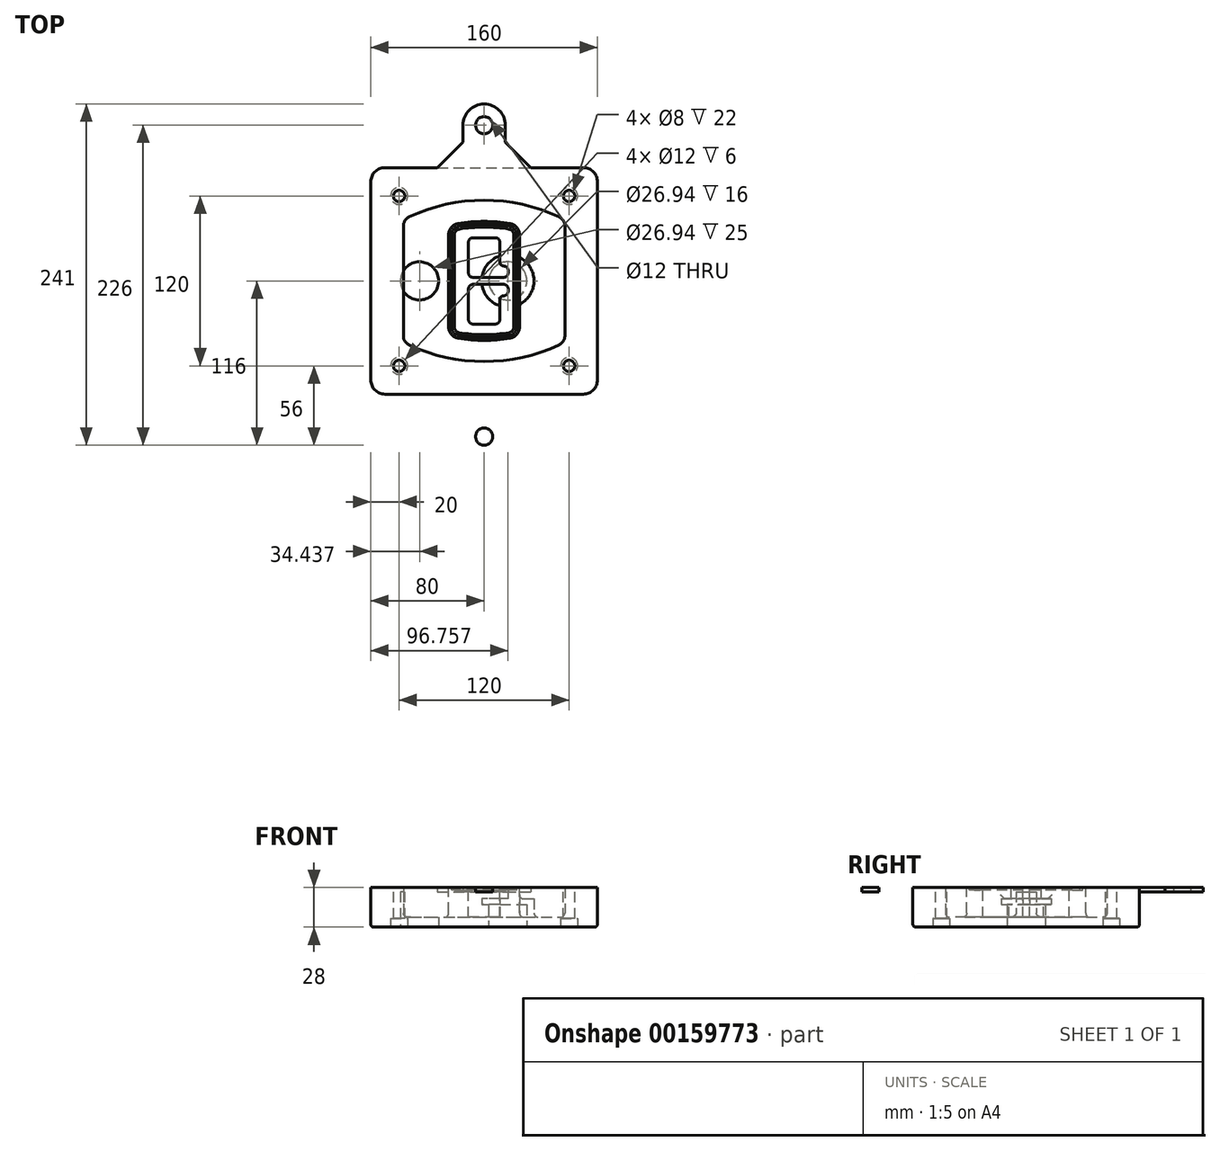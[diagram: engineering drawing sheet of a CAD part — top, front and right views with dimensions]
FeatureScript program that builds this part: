
annotation { "Feature Type Name" : "Feature", "Feature Type Description" : "" }
export const myFeature = defineFeature(function(context is Context, id is Id, definition is map)
    precondition{}
    {
        {
            var Q0;
            Q0=qCreatedBy(makeId("Top.planeOp"),FACE);
            var sketch = newSketch(context, id + "F0", { "sketchPlane" : qUnion([Q0])});
            skPoint(sketch, "E0.rect.middle", {"position": v(0, 0) * mm});
            skLineSegment(sketch, "E1.bottom", {"start": v(-70, -80) * mm, "end": v(70, -80) * mm});
            skLineSegment(sketch, "E1.top", {"start": v(-70, 80) * mm, "end": v(70, 80) * mm});
            skLineSegment(sketch, "E1.left", {"start": v(-80, -70) * mm, "end": v(-80, 70) * mm});
            skLineSegment(sketch, "E1.right", {"start": v(80, -70) * mm, "end": v(80, 70) * mm});
            skLineSegment(sketch, "E2", {"start": v(-80, 80) * mm, "end": v(80, -80) * mm, "construction": true});
            skLineSegment(sketch, "E3", {"start": v(80, 80) * mm, "end": v(-80, -80) * mm, "construction": true});
            skCircle(sketch, "E4", {"center": v(-60, 60) * mm, "radius": 4 * mm});
            skCircle(sketch, "E5", {"center": v(60, 60) * mm, "radius": 4 * mm});
            skCircle(sketch, "E6", {"center": v(60, -60) * mm, "radius": 4 * mm});
            skCircle(sketch, "E7", {"center": v(-60, -60) * mm, "radius": 4 * mm});
            skLineSegment(sketch, "E8", {"start": v(-60, 60) * mm, "end": v(60, 60) * mm, "construction": true});
            skLineSegment(sketch, "E9", {"start": v(60, 60) * mm, "end": v(60, -60) * mm, "construction": true});
            skLineSegment(sketch, "E10", {"start": v(60, -60) * mm, "end": v(-60, -60) * mm, "construction": true});
            skLineSegment(sketch, "E11", {"start": v(-60, -60) * mm, "end": v(-60, 60) * mm, "construction": true});
            skLineSegment(sketch, "E12", {"start": v(-60, 38.83) * mm, "end": v(-60, -38.83) * mm});
            skLineSegment(sketch, "E13", {"start": v(60, 38.83) * mm, "end": v(60, -38.83) * mm});
            skArc(sketch, "E14", {"start": v(54.26, 47.88) * mm, "mid": v(0, 60) * mm, "end": v(-54.26, 47.88) * mm});
            skArc(sketch, "E15", {"start": v(-54.26, -47.88) * mm, "mid": v(0, -60) * mm, "end": v(54.26, -47.88) * mm});
            skLineSegment(sketch, "E16", {"start": v(-60, 0) * mm, "end": v(60, 0) * mm, "construction": true});
            skPoint(sketch, "E17.visualSharp", {"position": v(-60, -45) * mm});
            skArc(sketch, "E17.filletArc", {"start": v(-60, -38.83) * mm, "mid": v(-58.44, -44.2) * mm, "end": v(-54.26, -47.88) * mm});
            skPoint(sketch, "E18.visualSharp", {"position": v(-60, 45) * mm});
            skArc(sketch, "E18.filletArc", {"start": v(-54.26, 47.88) * mm, "mid": v(-58.44, 44.2) * mm, "end": v(-60, 38.83) * mm});
            skPoint(sketch, "E19.visualSharp", {"position": v(60, 45) * mm});
            skArc(sketch, "E19.filletArc", {"start": v(60, 38.83) * mm, "mid": v(58.44, 44.2) * mm, "end": v(54.26, 47.88) * mm});
            skPoint(sketch, "E20.visualSharp", {"position": v(60, -45) * mm});
            skArc(sketch, "E20.filletArc", {"start": v(54.26, -47.88) * mm, "mid": v(58.44, -44.2) * mm, "end": v(60, -38.83) * mm});
            skPoint(sketch, "E21.visualSharp", {"position": v(-80, 80) * mm});
            skArc(sketch, "E21.filletArc", {"start": v(-70, 80) * mm, "mid": v(-77.07, 77.07) * mm, "end": v(-80, 70) * mm});
            skPoint(sketch, "E22.visualSharp", {"position": v(80, 80) * mm});
            skArc(sketch, "E22.filletArc", {"start": v(80, 70) * mm, "mid": v(77.07, 77.07) * mm, "end": v(70, 80) * mm});
            skPoint(sketch, "E23.visualSharp", {"position": v(80, -80) * mm});
            skArc(sketch, "E23.filletArc", {"start": v(70, -80) * mm, "mid": v(77.07, -77.07) * mm, "end": v(80, -70) * mm});
            skPoint(sketch, "E24.visualSharp", {"position": v(-80, -80) * mm});
            skArc(sketch, "E24.filletArc", {"start": v(-80, -70) * mm, "mid": v(-77.07, -77.07) * mm, "end": v(-70, -80) * mm});
            skArc(sketch, "E25.0", {"start": v(57, 38.83) * mm, "mid": v(55.9, 42.58) * mm, "end": v(52.98, 45.17) * mm});
            skLineSegment(sketch, "E25.1", {"start": v(57, 38.83) * mm, "end": v(57, -38.83) * mm});
            skArc(sketch, "E25.2", {"start": v(52.98, -45.17) * mm, "mid": v(55.9, -42.58) * mm, "end": v(57, -38.83) * mm});
            skArc(sketch, "E25.3", {"start": v(-52.98, -45.17) * mm, "mid": v(0, -57) * mm, "end": v(52.98, -45.17) * mm});
            skArc(sketch, "E25.4", {"start": v(-57, -38.83) * mm, "mid": v(-55.9, -42.58) * mm, "end": v(-52.98, -45.17) * mm});
            skArc(sketch, "E25.5", {"start": v(52.98, 45.17) * mm, "mid": v(0, 57) * mm, "end": v(-52.98, 45.17) * mm});
            skLineSegment(sketch, "E25.6", {"start": v(-57, 38.83) * mm, "end": v(-57, -38.83) * mm});
            skArc(sketch, "E25.7", {"start": v(-52.98, 45.17) * mm, "mid": v(-55.9, 42.58) * mm, "end": v(-57, 38.83) * mm});
            skArc(sketch, "E26.0", {"start": v(-55.96, 51.5) * mm, "mid": v(-61.82, 46.33) * mm, "end": v(-64, 38.83) * mm});
            skArc(sketch, "E26.1", {"start": v(55.96, 51.5) * mm, "mid": v(0, 64) * mm, "end": v(-55.96, 51.5) * mm});
            skArc(sketch, "E26.2", {"start": v(64, 38.83) * mm, "mid": v(61.82, 46.33) * mm, "end": v(55.96, 51.5) * mm});
            skLineSegment(sketch, "E26.3", {"start": v(64, 38.83) * mm, "end": v(64, -38.83) * mm});
            skArc(sketch, "E26.4", {"start": v(55.96, -51.5) * mm, "mid": v(61.82, -46.33) * mm, "end": v(64, -38.83) * mm});
            skLineSegment(sketch, "E26.5", {"start": v(-64, 38.83) * mm, "end": v(-64, -38.83) * mm});
            skArc(sketch, "E26.6", {"start": v(-55.96, -51.5) * mm, "mid": v(0, -64) * mm, "end": v(55.96, -51.5) * mm});
            skArc(sketch, "E26.7", {"start": v(-64, -38.83) * mm, "mid": v(-61.82, -46.33) * mm, "end": v(-55.96, -51.5) * mm});
            skSolve(sketch);
        }
        {
            var Q0;
            Q0=makeQuery(id+"F0.imprint","IMPRINT",FACE,{"disambiguationData":[TD([[makeQuery(id+"F0.imprint","IMPRINT",EDGE,{"derivedFrom":sQuery(id+"F0.wireOp",EDGE,"E1.bottom")}),1.0]])]});
            var Q1;
            Q1=makeQuery(id+"F0.imprint","IMPRINT",FACE,{"disambiguationData":[TD([[makeQuery(id+"F0.imprint","IMPRINT",EDGE,{"derivedFrom":sQuery(id+"F0.wireOp",EDGE,"E12")}),1.0]])]});
            var Q2;
            Q2=makeQuery(id+"F0.imprint","IMPRINT",FACE,{"disambiguationData":[TD([[makeQuery(id+"F0.imprint","IMPRINT",EDGE,{"derivedFrom":sQuery(id+"F0.wireOp",EDGE,"E25.0")}),1.0]])]});
            var Q3;
            Q3=makeQuery(id+"F0.imprint","IMPRINT",FACE,{"disambiguationData":[TD([[makeQuery(id+"F0.imprint","IMPRINT",EDGE,{"derivedFrom":sQuery(id+"F0.wireOp",EDGE,"E12")}),-1.0]])]});
            extrude(context, id + "F1", {"entities" : qUnion([Q0, Q1, Q2, Q3]), "oppositeDirection" : true, "depth" : 25 * mm});
        }
        {
            var Q0;
            Q0=makeQuery(id+"F0.imprint","IMPRINT",FACE,{"disambiguationData":[TD([[makeQuery(id+"F0.imprint","IMPRINT",EDGE,{"derivedFrom":sQuery(id+"F0.wireOp",EDGE,"E12")}),1.0]])]});
            extrude(context, id + "F2", {"entities" : qUnion([Q0]), "operationType" : NewBodyOperationType.ADD, "depth" : 3 * mm});
        }
        {
            var Q0;
            Q0=makeQuery(id+"F0.imprint","IMPRINT",FACE,{"disambiguationData":[TD([[makeQuery(id+"F0.imprint","IMPRINT",EDGE,{"derivedFrom":sQuery(id+"F0.wireOp",EDGE,"E25.0")}),1.0]])]});
            extrude(context, id + "F3", {"entities" : qUnion([Q0]), "operationType" : NewBodyOperationType.REMOVE, "oppositeDirection" : true, "depth" : 18 * mm});
        }
        {
            var Q0;
            Q0=makeQuery(id+"F2.opExtrude","CAP_FACE",FACE,{"disambiguationData":[OSD([sQuery(id+"F0.wireOp",EDGE,"E12"),sQuery(id+"F0.wireOp",EDGE,"E13"),sQuery(id+"F0.wireOp",EDGE,"E14"),sQuery(id+"F0.wireOp",EDGE,"E15"),sQuery(id+"F0.wireOp",EDGE,"E17.filletArc"),sQuery(id+"F0.wireOp",EDGE,"E18.filletArc"),sQuery(id+"F0.wireOp",EDGE,"E19.filletArc"),sQuery(id+"F0.wireOp",EDGE,"E20.filletArc"),sQuery(id+"F0.wireOp",EDGE,"E25.0"),sQuery(id+"F0.wireOp",EDGE,"E25.1"),sQuery(id+"F0.wireOp",EDGE,"E25.2"),sQuery(id+"F0.wireOp",EDGE,"E25.3"),sQuery(id+"F0.wireOp",EDGE,"E25.4"),sQuery(id+"F0.wireOp",EDGE,"E25.5"),sQuery(id+"F0.wireOp",EDGE,"E25.6"),sQuery(id+"F0.wireOp",EDGE,"E25.7")])],"isStart":false});
            var sketch = newSketch(context, id + "F4", { "sketchPlane" : qUnion([Q0])});
            skArc(sketch, "E27.0", {"start": v(-18.34, -40.45) * mm, "mid": v(0, -42) * mm, "end": v(18.34, -40.45) * mm});
            skArc(sketch, "E28.0", {"start": v(18.34, 40.45) * mm, "mid": v(0, 42) * mm, "end": v(-18.34, 40.45) * mm});
            skLineSegment(sketch, "E29", {"start": v(-25, 32.57) * mm, "end": v(-25, -32.57) * mm});
            skLineSegment(sketch, "E30", {"start": v(25, 32.57) * mm, "end": v(25, -32.57) * mm});
            skLineSegment(sketch, "E31", {"start": v(-25, 39.1) * mm, "end": v(25, 39.1) * mm, "construction": true});
            skLineSegment(sketch, "E32", {"start": v(-25, -39.1) * mm, "end": v(25, -39.1) * mm, "construction": true});
            skPoint(sketch, "E33.visualSharp", {"position": v(-25, 39.1) * mm});
            skArc(sketch, "E33.filletArc", {"start": v(-18.34, 40.45) * mm, "mid": v(-23.11, 37.73) * mm, "end": v(-25, 32.57) * mm});
            skPoint(sketch, "E34.visualSharp", {"position": v(25, 39.1) * mm});
            skArc(sketch, "E34.filletArc", {"start": v(25, 32.57) * mm, "mid": v(23.11, 37.73) * mm, "end": v(18.34, 40.45) * mm});
            skPoint(sketch, "E35.visualSharp", {"position": v(25, -39.1) * mm});
            skArc(sketch, "E35.filletArc", {"start": v(18.34, -40.45) * mm, "mid": v(23.11, -37.73) * mm, "end": v(25, -32.57) * mm});
            skPoint(sketch, "E36.visualSharp", {"position": v(-25, -39.1) * mm});
            skArc(sketch, "E36.filletArc", {"start": v(-25, -32.57) * mm, "mid": v(-23.11, -37.73) * mm, "end": v(-18.34, -40.45) * mm});
            skArc(sketch, "E37.0", {"start": v(52.98, 45.17) * mm, "mid": v(0, 57) * mm, "end": v(-52.98, 45.17) * mm});
            skArc(sketch, "E37.1", {"start": v(-52.98, 45.17) * mm, "mid": v(-55.9, 42.58) * mm, "end": v(-57, 38.83) * mm});
            skLineSegment(sketch, "E37.2", {"start": v(-57, 38.83) * mm, "end": v(-57, -38.83) * mm});
            skArc(sketch, "E37.3", {"start": v(-57, -38.83) * mm, "mid": v(-55.9, -42.58) * mm, "end": v(-52.98, -45.17) * mm});
            skArc(sketch, "E37.4", {"start": v(-52.98, -45.17) * mm, "mid": v(0, -57) * mm, "end": v(52.98, -45.17) * mm});
            skArc(sketch, "E37.5", {"start": v(52.98, -45.17) * mm, "mid": v(55.9, -42.58) * mm, "end": v(57, -38.83) * mm});
            skLineSegment(sketch, "E37.6", {"start": v(57, 38.83) * mm, "end": v(57, -38.83) * mm});
            skArc(sketch, "E37.7", {"start": v(57, 38.83) * mm, "mid": v(55.9, 42.58) * mm, "end": v(52.98, 45.17) * mm});
            skLineSegment(sketch, "E38.0", {"start": v(23, 32.57) * mm, "end": v(23, -32.57) * mm});
            skArc(sketch, "E38.1", {"start": v(18, -38.48) * mm, "mid": v(21.58, -36.44) * mm, "end": v(23, -32.57) * mm});
            skArc(sketch, "E38.2", {"start": v(-18, -38.48) * mm, "mid": v(0, -40) * mm, "end": v(18, -38.48) * mm});
            skArc(sketch, "E38.3", {"start": v(-23, -32.57) * mm, "mid": v(-21.58, -36.44) * mm, "end": v(-18, -38.48) * mm});
            skLineSegment(sketch, "E38.4", {"start": v(-23, 32.57) * mm, "end": v(-23, -32.57) * mm});
            skArc(sketch, "E38.5", {"start": v(23, 32.57) * mm, "mid": v(21.58, 36.44) * mm, "end": v(18, 38.48) * mm});
            skArc(sketch, "E38.6", {"start": v(-18, 38.48) * mm, "mid": v(-21.58, 36.44) * mm, "end": v(-23, 32.57) * mm});
            skArc(sketch, "E38.7", {"start": v(18, 38.48) * mm, "mid": v(0, 40) * mm, "end": v(-18, 38.48) * mm});
            skArc(sketch, "E39.0", {"start": v(21, 32.57) * mm, "mid": v(20.06, 35.15) * mm, "end": v(17.67, 36.5) * mm});
            skLineSegment(sketch, "E39.1", {"start": v(21, 32.57) * mm, "end": v(21, -32.57) * mm});
            skArc(sketch, "E39.2", {"start": v(17.67, -36.5) * mm, "mid": v(20.06, -35.15) * mm, "end": v(21, -32.57) * mm});
            skArc(sketch, "E39.3", {"start": v(-17.67, -36.5) * mm, "mid": v(0, -38) * mm, "end": v(17.67, -36.5) * mm});
            skArc(sketch, "E39.4", {"start": v(-21, -32.57) * mm, "mid": v(-20.06, -35.15) * mm, "end": v(-17.67, -36.5) * mm});
            skArc(sketch, "E39.5", {"start": v(17.67, 36.5) * mm, "mid": v(0, 38) * mm, "end": v(-17.67, 36.5) * mm});
            skLineSegment(sketch, "E39.6", {"start": v(-21, 32.57) * mm, "end": v(-21, -32.57) * mm});
            skArc(sketch, "E39.7", {"start": v(-17.67, 36.5) * mm, "mid": v(-20.06, 35.15) * mm, "end": v(-21, 32.57) * mm});
            skLineSegment(sketch, "E40", {"start": v(-25, 0) * mm, "end": v(25, 0) * mm, "construction": true});
            skLineSegment(sketch, "E41", {"start": v(-11, 5.5) * mm, "end": v(-11, 27.5) * mm});
            skLineSegment(sketch, "E42", {"start": v(-8, 30.5) * mm, "end": v(8, 30.5) * mm});
            skLineSegment(sketch, "E43", {"start": v(11, 27.5) * mm, "end": v(11, 13.5) * mm});
            skLineSegment(sketch, "E44", {"start": v(14, 10.5) * mm, "end": v(14, 10.5) * mm});
            skLineSegment(sketch, "E45", {"start": v(17, 7.5) * mm, "end": v(17, 5.5) * mm});
            skLineSegment(sketch, "E46", {"start": v(14, 2.5) * mm, "end": v(-8, 2.5) * mm});
            skPoint(sketch, "E47.visualSharp", {"position": v(-11, 30.5) * mm});
            skArc(sketch, "E47.filletArc", {"start": v(-8, 30.5) * mm, "mid": v(-10.12, 29.62) * mm, "end": v(-11, 27.5) * mm});
            skPoint(sketch, "E48.visualSharp", {"position": v(11, 30.5) * mm});
            skArc(sketch, "E48.filletArc", {"start": v(11, 27.5) * mm, "mid": v(10.12, 29.62) * mm, "end": v(8, 30.5) * mm});
            skPoint(sketch, "E49.visualSharp", {"position": v(11, 10.5) * mm});
            skArc(sketch, "E49.filletArc", {"start": v(11, 13.5) * mm, "mid": v(11.88, 11.38) * mm, "end": v(14, 10.5) * mm});
            skPoint(sketch, "E50.visualSharp", {"position": v(17, 10.5) * mm});
            skArc(sketch, "E50.filletArc", {"start": v(17, 7.5) * mm, "mid": v(16.12, 9.62) * mm, "end": v(14, 10.5) * mm});
            skPoint(sketch, "E51.visualSharp", {"position": v(17, 2.5) * mm});
            skArc(sketch, "E51.filletArc", {"start": v(14, 2.5) * mm, "mid": v(16.12, 3.38) * mm, "end": v(17, 5.5) * mm});
            skPoint(sketch, "E52.visualSharp", {"position": v(-11, 2.5) * mm});
            skArc(sketch, "E52.filletArc", {"start": v(-11, 5.5) * mm, "mid": v(-10.12, 3.38) * mm, "end": v(-8, 2.5) * mm});
            skLineSegment(sketch, "E53.0.MirrorCS", {"start": v(14, -2.5) * mm, "end": v(-8, -2.5) * mm});
            skArc(sketch, "E54.0.MirrorCS", {"start": v(-11, -5.5) * mm, "mid": v(-10.12, -3.38) * mm, "end": v(-8, -2.5) * mm});
            skLineSegment(sketch, "E55.0.MirrorCS", {"start": v(-11, -5.5) * mm, "end": v(-11, -27.5) * mm});
            skArc(sketch, "E56.0.MirrorCS", {"start": v(-8, -30.5) * mm, "mid": v(-10.12, -29.62) * mm, "end": v(-11, -27.5) * mm});
            skLineSegment(sketch, "E57.0.MirrorCS", {"start": v(-8, -30.5) * mm, "end": v(8, -30.5) * mm});
            skArc(sketch, "E58.0.MirrorCS", {"start": v(11, -27.5) * mm, "mid": v(10.12, -29.62) * mm, "end": v(8, -30.5) * mm});
            skLineSegment(sketch, "E59.0.MirrorCS", {"start": v(11, -27.5) * mm, "end": v(11, -13.5) * mm});
            skArc(sketch, "E60.0.MirrorCS", {"start": v(11, -13.5) * mm, "mid": v(11.88, -11.38) * mm, "end": v(14, -10.5) * mm});
            skArc(sketch, "E61.0.MirrorCS", {"start": v(17, -7.5) * mm, "mid": v(16.12, -9.62) * mm, "end": v(14, -10.5) * mm});
            skLineSegment(sketch, "E62.0.MirrorCS", {"start": v(17, -7.5) * mm, "end": v(17, -5.5) * mm});
            skArc(sketch, "E63.0.MirrorCS", {"start": v(14, -2.5) * mm, "mid": v(16.12, -3.38) * mm, "end": v(17, -5.5) * mm});
            skSolve(sketch);
        }
        {
            var Q0;
            Q0=makeQuery(id+"F4.imprint","IMPRINT",FACE,{"disambiguationData":[TD([[makeQuery(id+"F4.imprint","IMPRINT",EDGE,{"derivedFrom":sQuery(id+"F4.wireOp",EDGE,"E27.0")}),1.0]])]});
            var Q1;
            Q1=makeQuery(id+"F4.imprint","IMPRINT",FACE,{"disambiguationData":[TD([[makeQuery(id+"F4.imprint","IMPRINT",EDGE,{"derivedFrom":sQuery(id+"F4.wireOp",EDGE,"E38.0")}),-1.0]])]});
            var Q2;
            Q2=makeQuery(id+"F4.imprint","IMPRINT",FACE,{"disambiguationData":[TD([[makeQuery(id+"F4.imprint","IMPRINT",EDGE,{"derivedFrom":sQuery(id+"F4.wireOp",EDGE,"E39.0")}),1.0]])]});
            extrude(context, id + "F5", {"entities" : qUnion([Q0, Q1, Q2]), "operationType" : NewBodyOperationType.ADD, "endBound" : BoundingType.UP_TO_NEXT, "oppositeDirection" : true, "depth" : 25 * mm});
        }
        {
            var Q0;
            Q0=makeQuery(id+"F4.imprint","IMPRINT",FACE,{"disambiguationData":[TD([[makeQuery(id+"F4.imprint","IMPRINT",EDGE,{"derivedFrom":sQuery(id+"F4.wireOp",EDGE,"E38.0")}),-1.0]])]});
            extrude(context, id + "F6", {"entities" : qUnion([Q0]), "operationType" : NewBodyOperationType.REMOVE, "oppositeDirection" : true, "depth" : 2 * mm});
        }
        {
            var Q0;
            Q0=makeQuery(id+"F1.opExtrude","CAP_FACE",FACE,{"disambiguationData":[OSD([sQuery(id+"F0.wireOp",EDGE,"E1.bottom"),sQuery(id+"F0.wireOp",EDGE,"E1.top"),sQuery(id+"F0.wireOp",EDGE,"E1.left"),sQuery(id+"F0.wireOp",EDGE,"E1.right"),sQuery(id+"F0.wireOp",EDGE,"E4"),sQuery(id+"F0.wireOp",EDGE,"E5"),sQuery(id+"F0.wireOp",EDGE,"E6"),sQuery(id+"F0.wireOp",EDGE,"E7"),sQuery(id+"F0.wireOp",EDGE,"E21.filletArc"),sQuery(id+"F0.wireOp",EDGE,"E22.filletArc"),sQuery(id+"F0.wireOp",EDGE,"E23.filletArc"),sQuery(id+"F0.wireOp",EDGE,"E24.filletArc")])],"isStart":false});
            var sketch = newSketch(context, id + "F7", { "sketchPlane" : qUnion([Q0])});
            skCircle(sketch, "E64", {"center": v(16.76, 0) * mm, "radius": 13.47 * mm});
            skCircle(sketch, "E65", {"center": v(-45.56, 0) * mm, "radius": 13.47 * mm});
            skLineSegment(sketch, "E66", {"start": v(80, 0) * mm, "end": v(-80, 0) * mm});
            skCircle(sketch, "E67", {"center": v(16.76, 0) * mm, "radius": 18.47 * mm});
            skCircle(sketch, "E68", {"center": v(60, -60) * mm, "radius": 6 * mm});
            skCircle(sketch, "E69", {"center": v(-60, -60) * mm, "radius": 6 * mm});
            skCircle(sketch, "E70", {"center": v(-60, 60) * mm, "radius": 6 * mm});
            skCircle(sketch, "E71", {"center": v(60, 60) * mm, "radius": 6 * mm});
            skSolve(sketch);
        }
        {
            var Q0;
            {var subQ1=sQuery(id+"F7.wireOp",EDGE,"E66");var subQ4=sQuery(id+"F7.wireOp",EDGE,"E64");var subQ6=makeQuery(id+"F7.imprint","INTERSECT",VERTEX,{"disambiguationData":[OD(0.0)],"derivedFrom":[subQ4,subQ1]});Q0=makeQuery(id+"F7.imprint","IMPRINT",FACE,{"disambiguationData":[TD([[makeQuery(id+"F7.imprint","IMPRINT",EDGE,{"disambiguationData":[TD([[subQ6,-1.0]])],"derivedFrom":subQ4}),-1.0]])]});}
            var Q1;
            {var subQ0=sQuery(id+"F7.wireOp",EDGE,"E66");var subQ1=sQuery(id+"F7.wireOp",EDGE,"E64");var subQ3=makeQuery(id+"F7.imprint","INTERSECT",VERTEX,{"disambiguationData":[OD(0.0)],"derivedFrom":[subQ1,subQ0]});Q1=makeQuery(id+"F7.imprint","IMPRINT",FACE,{"disambiguationData":[TD([[makeQuery(id+"F7.imprint","IMPRINT",EDGE,{"disambiguationData":[TD([[subQ3,-1.0]])],"derivedFrom":subQ1}),1.0]])]});}
            var Q2;
            {var subQ0=sQuery(id+"F7.wireOp",EDGE,"E66");var subQ1=sQuery(id+"F7.wireOp",EDGE,"E64");var subQ3=makeQuery(id+"F7.imprint","INTERSECT",VERTEX,{"disambiguationData":[OD(0.0)],"derivedFrom":[subQ1,subQ0]});Q2=makeQuery(id+"F7.imprint","IMPRINT",FACE,{"disambiguationData":[TD([[makeQuery(id+"F7.imprint","IMPRINT",EDGE,{"disambiguationData":[TD([[subQ3,1.0]])],"derivedFrom":subQ1}),1.0]])]});}
            var Q3;
            {var subQ1=sQuery(id+"F7.wireOp",EDGE,"E66");var subQ4=sQuery(id+"F7.wireOp",EDGE,"E64");var subQ6=makeQuery(id+"F7.imprint","INTERSECT",VERTEX,{"disambiguationData":[OD(0.0)],"derivedFrom":[subQ4,subQ1]});Q3=makeQuery(id+"F7.imprint","IMPRINT",FACE,{"disambiguationData":[TD([[makeQuery(id+"F7.imprint","IMPRINT",EDGE,{"disambiguationData":[TD([[subQ6,1.0]])],"derivedFrom":subQ4}),-1.0]])]});}
            extrude(context, id + "F8", {"entities" : qUnion([Q0, Q1, Q2, Q3]), "operationType" : NewBodyOperationType.ADD, "oppositeDirection" : true, "depth" : 20 * mm});
        }
        {
            var Q0;
            {var subQ0=sQuery(id+"F7.wireOp",EDGE,"E66");var subQ1=sQuery(id+"F7.wireOp",EDGE,"E64");var subQ3=makeQuery(id+"F7.imprint","INTERSECT",VERTEX,{"disambiguationData":[OD(0.0)],"derivedFrom":[subQ1,subQ0]});Q0=makeQuery(id+"F7.imprint","IMPRINT",FACE,{"disambiguationData":[TD([[makeQuery(id+"F7.imprint","IMPRINT",EDGE,{"disambiguationData":[TD([[subQ3,-1.0]])],"derivedFrom":subQ1}),1.0]])]});}
            var Q1;
            {var subQ0=sQuery(id+"F7.wireOp",EDGE,"E66");var subQ1=sQuery(id+"F7.wireOp",EDGE,"E64");var subQ3=makeQuery(id+"F7.imprint","INTERSECT",VERTEX,{"disambiguationData":[OD(0.0)],"derivedFrom":[subQ1,subQ0]});Q1=makeQuery(id+"F7.imprint","IMPRINT",FACE,{"disambiguationData":[TD([[makeQuery(id+"F7.imprint","IMPRINT",EDGE,{"disambiguationData":[TD([[subQ3,1.0]])],"derivedFrom":subQ1}),1.0]])]});}
            extrude(context, id + "F9", {"entities" : qUnion([Q0, Q1]), "operationType" : NewBodyOperationType.REMOVE, "oppositeDirection" : true, "depth" : 16 * mm});
        }
        {
            var Q0;
            {var subQ0=sQuery(id+"F7.wireOp",EDGE,"E66");var subQ1=sQuery(id+"F7.wireOp",EDGE,"E65");var subQ3=makeQuery(id+"F7.imprint","INTERSECT",VERTEX,{"disambiguationData":[OD(0.0)],"derivedFrom":[subQ1,subQ0]});Q0=makeQuery(id+"F7.imprint","IMPRINT",FACE,{"disambiguationData":[TD([[makeQuery(id+"F7.imprint","IMPRINT",EDGE,{"disambiguationData":[TD([[subQ3,-1.0]])],"derivedFrom":subQ1}),1.0]])]});}
            var Q1;
            {var subQ0=sQuery(id+"F7.wireOp",EDGE,"E66");var subQ1=sQuery(id+"F7.wireOp",EDGE,"E65");var subQ3=makeQuery(id+"F7.imprint","INTERSECT",VERTEX,{"disambiguationData":[OD(0.0)],"derivedFrom":[subQ1,subQ0]});Q1=makeQuery(id+"F7.imprint","IMPRINT",FACE,{"disambiguationData":[TD([[makeQuery(id+"F7.imprint","IMPRINT",EDGE,{"disambiguationData":[TD([[subQ3,1.0]])],"derivedFrom":subQ1}),1.0]])]});}
            extrude(context, id + "F10", {"entities" : qUnion([Q0, Q1]), "operationType" : NewBodyOperationType.REMOVE, "oppositeDirection" : true, "depth" : 25 * mm});
        }
        {
            var Q0;
            Q0=makeQuery(id+"F7.imprint","IMPRINT",FACE,{"disambiguationData":[TD([[makeQuery(id+"F7.imprint","IMPRINT",EDGE,{"derivedFrom":sQuery(id+"F7.wireOp",EDGE,"E68")}),1.0]])]});
            var Q1;
            Q1=makeQuery(id+"F7.imprint","IMPRINT",FACE,{"disambiguationData":[TD([[makeQuery(id+"F7.imprint","IMPRINT",EDGE,{"derivedFrom":makeQuery(id+"F1.opExtrude","CAP_EDGE",EDGE,{"disambiguationData":[OSD([sQuery(id+"F0.wireOp",EDGE,"E5")])],"isStart":false})}),-1.0]])]});
            var Q2;
            Q2=makeQuery(id+"F7.imprint","IMPRINT",FACE,{"disambiguationData":[TD([[makeQuery(id+"F7.imprint","IMPRINT",EDGE,{"derivedFrom":sQuery(id+"F7.wireOp",EDGE,"E69")}),1.0]])]});
            var Q3;
            Q3=makeQuery(id+"F7.imprint","IMPRINT",FACE,{"disambiguationData":[TD([[makeQuery(id+"F7.imprint","IMPRINT",EDGE,{"derivedFrom":makeQuery(id+"F1.opExtrude","CAP_EDGE",EDGE,{"disambiguationData":[OSD([sQuery(id+"F0.wireOp",EDGE,"E4")])],"isStart":false})}),-1.0]])]});
            var Q4;
            Q4=makeQuery(id+"F7.imprint","IMPRINT",FACE,{"disambiguationData":[TD([[makeQuery(id+"F7.imprint","IMPRINT",EDGE,{"derivedFrom":sQuery(id+"F7.wireOp",EDGE,"E70")}),1.0]])]});
            var Q5;
            Q5=makeQuery(id+"F7.imprint","IMPRINT",FACE,{"disambiguationData":[TD([[makeQuery(id+"F7.imprint","IMPRINT",EDGE,{"derivedFrom":makeQuery(id+"F1.opExtrude","CAP_EDGE",EDGE,{"disambiguationData":[OSD([sQuery(id+"F0.wireOp",EDGE,"E7")])],"isStart":false})}),-1.0]])]});
            var Q6;
            Q6=makeQuery(id+"F7.imprint","IMPRINT",FACE,{"disambiguationData":[TD([[makeQuery(id+"F7.imprint","IMPRINT",EDGE,{"derivedFrom":sQuery(id+"F7.wireOp",EDGE,"E71")}),1.0]])]});
            var Q7;
            Q7=makeQuery(id+"F7.imprint","IMPRINT",FACE,{"disambiguationData":[TD([[makeQuery(id+"F7.imprint","IMPRINT",EDGE,{"derivedFrom":makeQuery(id+"F1.opExtrude","CAP_EDGE",EDGE,{"disambiguationData":[OSD([sQuery(id+"F0.wireOp",EDGE,"E6")])],"isStart":false})}),-1.0]])]});
            extrude(context, id + "F11", {"entities" : qUnion([Q0, Q1, Q2, Q3, Q4, Q5, Q6, Q7]), "operationType" : NewBodyOperationType.REMOVE, "oppositeDirection" : true, "depth" : 6 * mm});
        }
        {
            var Q0;
            Q0=makeQuery(id+"F9.boolean.opBoolean","COPY",FACE,{"derivedFrom":makeQuery(id+"F9.opExtrude","CAP_FACE",FACE,{"disambiguationData":[OSD([sQuery(id+"F7.wireOp",EDGE,"E64")])],"isStart":false})});
            var sketch = newSketch(context, id + "F12", { "sketchPlane" : qUnion([Q0])});
            skArc(sketch, "E72.0", {"start": v(11, 17.55) * mm, "mid": v(2.57, 11.82) * mm, "end": v(-1.54, 2.5) * mm});
            skArc(sketch, "E72.1", {"start": v(-1.54, -2.5) * mm, "mid": v(2.57, -11.82) * mm, "end": v(11, -17.55) * mm});
            skLineSegment(sketch, "E73", {"start": v(-1.54, -2.5) * mm, "end": v(14, -2.5) * mm});
            skLineSegment(sketch, "E74.0", {"start": v(14, 2.5) * mm, "end": v(-1.54, 2.5) * mm});
            skArc(sketch, "E74.1", {"start": v(14, 2.5) * mm, "mid": v(16.12, 3.38) * mm, "end": v(17, 5.5) * mm});
            skLineSegment(sketch, "E74.2", {"start": v(17, 7.5) * mm, "end": v(17, 5.5) * mm});
            skArc(sketch, "E74.3", {"start": v(17, 7.5) * mm, "mid": v(16.12, 9.62) * mm, "end": v(14, 10.5) * mm});
            skArc(sketch, "E74.4", {"start": v(11, 13.5) * mm, "mid": v(11.88, 11.38) * mm, "end": v(14, 10.5) * mm});
            skLineSegment(sketch, "E74.5", {"start": v(11, 17.55) * mm, "end": v(11, 13.5) * mm});
            skLineSegment(sketch, "E74.7", {"start": v(14, -2.5) * mm, "end": v(-1.54, -2.5) * mm});
            skArc(sketch, "E74.8", {"start": v(14, -2.5) * mm, "mid": v(16.12, -3.38) * mm, "end": v(17, -5.5) * mm});
            skLineSegment(sketch, "E74.9", {"start": v(17, -7.5) * mm, "end": v(17, -5.5) * mm});
            skArc(sketch, "E74.10", {"start": v(17, -7.5) * mm, "mid": v(16.12, -9.62) * mm, "end": v(14, -10.5) * mm});
            skArc(sketch, "E74.11", {"start": v(11, -13.5) * mm, "mid": v(11.88, -11.38) * mm, "end": v(14, -10.5) * mm});
            skLineSegment(sketch, "E74.12", {"start": v(11, -17.55) * mm, "end": v(11, -13.5) * mm});
            skPoint(sketch, "E75.orphan", {"position": v(11, -27.5) * mm});
            skPoint(sketch, "E76.orphan", {"position": v(-8, -2.5) * mm});
            skPoint(sketch, "E77.orphan", {"position": v(-8, 2.5) * mm});
            skPoint(sketch, "E78.orphan", {"position": v(11, 27.5) * mm});
            skSolve(sketch);
        }
        {
            var Q0;
            {var subQ7=sQuery(id+"F12.wireOp",EDGE,"E72.0");var subQ14=sQuery(id+"F12.wireOp",EDGE,"E72.1");var subQ16=sQuery(id+"F12.wireOp",EDGE,"E74.1");var subQ18=sQuery(id+"F12.wireOp",EDGE,"E74.8");Q0=qUnion([makeQuery(id+"F12.imprint","IMPRINT",FACE,{"disambiguationData":[TD([[makeQuery(id+"F12.imprint","IMPRINT",EDGE,{"derivedFrom":subQ7}),1.0]])]}),makeQuery(id+"F12.imprint","IMPRINT",FACE,{"disambiguationData":[TD([[makeQuery(id+"F12.imprint","IMPRINT",EDGE,{"derivedFrom":subQ14}),1.0]])]}),makeQuery(id+"F12.imprint","IMPRINT",FACE,{"disambiguationData":[TD([[makeQuery(id+"F12.imprint","IMPRINT",EDGE,{"derivedFrom":subQ16}),1.0]])]}),makeQuery(id+"F12.imprint","IMPRINT",FACE,{"disambiguationData":[TD([[makeQuery(id+"F12.imprint","IMPRINT",EDGE,{"derivedFrom":subQ18}),-1.0]])]})]);}
            var Q1;
            Q1=makeQuery(id+"F5.boolean.opBoolean","SPLIT",FACE,{"disambiguationData":[TD([makeQuery(id+"F5.opExtrude","SWEPT_FACE",FACE,{"disambiguationData":[OSD([sQuery(id+"F4.wireOp",EDGE,"E41")])]})])],"derivedFrom":makeQuery(id+"F3.boolean.opBoolean","COPY",FACE,{"derivedFrom":makeQuery(id+"F3.opExtrude","CAP_FACE",FACE,{"disambiguationData":[OSD([sQuery(id+"F0.wireOp",EDGE,"E25.0"),sQuery(id+"F0.wireOp",EDGE,"E25.1"),sQuery(id+"F0.wireOp",EDGE,"E25.2"),sQuery(id+"F0.wireOp",EDGE,"E25.3"),sQuery(id+"F0.wireOp",EDGE,"E25.4"),sQuery(id+"F0.wireOp",EDGE,"E25.5"),sQuery(id+"F0.wireOp",EDGE,"E25.6"),sQuery(id+"F0.wireOp",EDGE,"E25.7")])],"isStart":false})})});
            extrude(context, id + "F13", {"entities" : qUnion([Q0]), "operationType" : NewBodyOperationType.REMOVE, "endBound" : BoundingType.UP_TO_SURFACE, "endBoundEntityFace" : qUnion([Q1]), "depth" : 25 * mm});
        }
        {
            var Q0;
            Q0=makeQuery(id+"F3.boolean.opBoolean","COPY",EDGE,{"derivedFrom":makeQuery(id+"F3.opExtrude","CAP_EDGE",EDGE,{"disambiguationData":[OSD([sQuery(id+"F0.wireOp",EDGE,"E25.6")])],"isStart":false})});
            var Q1;
            Q1=makeQuery(id+"F8.boolean.opBoolean","INTERSECT",EDGE,{"derivedFrom":[makeQuery(id+"F5.opExtrude","SWEPT_FACE",FACE,{"disambiguationData":[OSD([sQuery(id+"F4.wireOp",EDGE,"E30")])]}),makeQuery(id+"F8.opExtrude","CAP_FACE",FACE,{"disambiguationData":[OSD([sQuery(id+"F7.wireOp",EDGE,"E67")])],"isStart":false})]});
            var Q2;
            Q2=makeQuery(id+"F8.boolean.opBoolean","INTERSECT",EDGE,{"disambiguationData":[OD(1.0)],"derivedFrom":[makeQuery(id+"F5.opExtrude","SWEPT_FACE",FACE,{"disambiguationData":[OSD([sQuery(id+"F4.wireOp",EDGE,"E30")])]}),makeQuery(id+"F8.opExtrude","SWEPT_FACE",FACE,{"disambiguationData":[OSD([sQuery(id+"F7.wireOp",EDGE,"E67")])]})]});
            var Q3;
            {var subQ0=sQuery(id+"F4.wireOp",EDGE,"E30");Q3=makeQuery(id+"F8.boolean.opBoolean","SPLIT",EDGE,{"disambiguationData":[TD([makeQuery(id+"F5.opExtrude","SWEPT_FACE",FACE,{"disambiguationData":[OSD([sQuery(id+"F4.wireOp",EDGE,"E35.filletArc")])]})])],"derivedFrom":makeQuery(id+"F5.opExtrude","CAP_EDGE",EDGE,{"disambiguationData":[OSD([subQ0])],"isStart":false})});}
            var Q4;
            {var subQ0=sQuery(id+"F0.wireOp",EDGE,"E25.7");var subQ1=sQuery(id+"F0.wireOp",EDGE,"E25.1");var subQ2=sQuery(id+"F0.wireOp",EDGE,"E25.6");var subQ3=sQuery(id+"F0.wireOp",EDGE,"E25.5");var subQ4=sQuery(id+"F0.wireOp",EDGE,"E25.4");var subQ5=sQuery(id+"F0.wireOp",EDGE,"E25.0");var subQ6=sQuery(id+"F0.wireOp",EDGE,"E25.2");var subQ7=sQuery(id+"F0.wireOp",EDGE,"E25.3");Q4=makeQuery(id+"F8.boolean.opBoolean","INTERSECT",EDGE,{"derivedFrom":[makeQuery(id+"F5.boolean.opBoolean","SPLIT",FACE,{"disambiguationData":[TD([makeQuery(id+"F2.opExtrude","SWEPT_FACE",FACE,{"disambiguationData":[OSD([subQ5])]})])],"derivedFrom":makeQuery(id+"F3.boolean.opBoolean","COPY",FACE,{"derivedFrom":makeQuery(id+"F3.opExtrude","CAP_FACE",FACE,{"disambiguationData":[OSD([subQ5,subQ1,subQ6,subQ7,subQ4,subQ3,subQ2,subQ0])],"isStart":false})})}),makeQuery(id+"F8.opExtrude","SWEPT_FACE",FACE,{"disambiguationData":[OSD([sQuery(id+"F7.wireOp",EDGE,"E67")])]})]});}
            var Q5;
            Q5=makeQuery(id+"F8.boolean.opBoolean","INTERSECT",EDGE,{"disambiguationData":[OD(0.0)],"derivedFrom":[makeQuery(id+"F5.opExtrude","SWEPT_FACE",FACE,{"disambiguationData":[OSD([sQuery(id+"F4.wireOp",EDGE,"E30")])]}),makeQuery(id+"F8.opExtrude","SWEPT_FACE",FACE,{"disambiguationData":[OSD([sQuery(id+"F7.wireOp",EDGE,"E67")])]})]});
            fillet(context, id + "F14", {"entities" : qUnion([Q0, Q1, Q2, Q3, Q4, Q5]), "radius" : 3 * mm, "tangentPropagation" : true, "allowEdgeOverflow" : false});
        }
        {
            var Q0;
            Q0=makeQuery(id+"F1.opExtrude","CAP_EDGE",EDGE,{"disambiguationData":[OSD([sQuery(id+"F0.wireOp",EDGE,"E1.bottom")])],"isStart":false});
            fillet(context, id + "F15", {"entities" : qUnion([Q0]), "radius" : 2 * mm, "tangentPropagation" : true, "allowEdgeOverflow" : false});
        }
        {
            var Q0;
            {var subQ0=sQuery(id+"F0.wireOp",EDGE,"E22.filletArc");var subQ1=sQuery(id+"F0.wireOp",EDGE,"E7");var subQ2=sQuery(id+"F0.wireOp",EDGE,"E6");var subQ3=sQuery(id+"F0.wireOp",EDGE,"E5");var subQ4=sQuery(id+"F0.wireOp",EDGE,"E4");var subQ5=sQuery(id+"F0.wireOp",EDGE,"E1.bottom");var subQ6=sQuery(id+"F0.wireOp",EDGE,"E21.filletArc");var subQ7=sQuery(id+"F0.wireOp",EDGE,"E1.top");var subQ8=sQuery(id+"F0.wireOp",EDGE,"E1.left");var subQ9=sQuery(id+"F0.wireOp",EDGE,"E1.right");var subQ10=sQuery(id+"F0.wireOp",EDGE,"E23.filletArc");var subQ11=sQuery(id+"F0.wireOp",EDGE,"E24.filletArc");Q0=makeQuery(id+"F2.boolean.opBoolean","SPLIT",FACE,{"disambiguationData":[TD([makeQuery(id+"F1.opExtrude","SWEPT_FACE",FACE,{"disambiguationData":[OSD([subQ5])]})])],"derivedFrom":makeQuery(id+"F1.opExtrude","CAP_FACE",FACE,{"disambiguationData":[OSD([subQ5,subQ7,subQ8,subQ9,subQ4,subQ3,subQ2,subQ1,subQ6,subQ0,subQ10,subQ11])],"isStart":true})});}
            var sketch = newSketch(context, id + "F16", { "sketchPlane" : qUnion([Q0])});
            skLineSegment(sketch, "E79", {"start": v(0, 110) * mm, "end": v(0, 80) * mm, "construction": true});
            skPoint(sketch, "E79.startSnap0", {"position": v(0, 80) * mm});
            skCircle(sketch, "E80", {"center": v(0, 110) * mm, "radius": 6 * mm});
            skLineSegment(sketch, "E81", {"start": v(-33, 80) * mm, "end": v(-15, 98) * mm});
            skLineSegment(sketch, "E82", {"start": v(-15, 98) * mm, "end": v(-15, 110) * mm});
            skLineSegment(sketch, "E83", {"start": v(15, 110) * mm, "end": v(15, 98) * mm});
            skLineSegment(sketch, "E84", {"start": v(15, 98) * mm, "end": v(33, 80) * mm});
            skArc(sketch, "E85", {"start": v(15, 110) * mm, "mid": v(0, 125) * mm, "end": v(-15, 110) * mm});
            skLineSegment(sketch, "E86", {"start": v(-80, 0) * mm, "end": v(80, 0) * mm, "construction": true});
            skCircle(sketch, "E87.MirrorC", {"center": v(0, -110) * mm, "radius": 6 * mm});
            skArc(sketch, "E88.MirrorCS", {"start": v(15, -110) * mm, "mid": v(0, -125) * mm, "end": v(-15, -110) * mm});
            skLineSegment(sketch, "E89.MirrorCS", {"start": v(0, -110) * mm, "end": v(0, -80) * mm, "construction": true});
            skLineSegment(sketch, "E90.MirrorCS", {"start": v(15, -110) * mm, "end": v(15, -98) * mm});
            skLineSegment(sketch, "E91.MirrorCS", {"start": v(15, -98) * mm, "end": v(33, -80) * mm});
            skLineSegment(sketch, "E92.MirrorCS", {"start": v(-15, -98) * mm, "end": v(-15, -110) * mm});
            skLineSegment(sketch, "E93.MirrorCS", {"start": v(-33, -80) * mm, "end": v(-15, -98) * mm});
            skSolve(sketch);
        }
        {
            var Q0;
            Q0=makeQuery(id+"F16.imprint","IMPRINT",FACE,{"disambiguationData":[TD([[makeQuery(id+"F16.imprint","IMPRINT",EDGE,{"derivedFrom":makeQuery(id+"F1.opExtrude","CAP_EDGE",EDGE,{"disambiguationData":[OSD([sQuery(id+"F0.wireOp",EDGE,"E1.left")])],"isStart":true})}),-1.0]])]});
            var Q1;
            Q1=makeQuery(id+"F16.imprint","IMPRINT",FACE,{"disambiguationData":[TD([[makeQuery(id+"F16.imprint","IMPRINT",EDGE,{"derivedFrom":sQuery(id+"F16.wireOp",EDGE,"E80")}),-1.0]])]});
            var Q2;
            Q2=makeQuery(id+"F16.imprint","IMPRINT",FACE,{"disambiguationData":[TD([[makeQuery(id+"F16.imprint","IMPRINT",EDGE,{"derivedFrom":sQuery(id+"F16.wireOp",EDGE,"E87.MirrorC")}),1.0]])]});
            var Q3;
            Q3=makeQuery(id+"F2.opExtrude","CAP_FACE",FACE,{"disambiguationData":[OSD([sQuery(id+"F0.wireOp",EDGE,"E12"),sQuery(id+"F0.wireOp",EDGE,"E13"),sQuery(id+"F0.wireOp",EDGE,"E14"),sQuery(id+"F0.wireOp",EDGE,"E15"),sQuery(id+"F0.wireOp",EDGE,"E17.filletArc"),sQuery(id+"F0.wireOp",EDGE,"E18.filletArc"),sQuery(id+"F0.wireOp",EDGE,"E19.filletArc"),sQuery(id+"F0.wireOp",EDGE,"E20.filletArc"),sQuery(id+"F0.wireOp",EDGE,"E25.0"),sQuery(id+"F0.wireOp",EDGE,"E25.1"),sQuery(id+"F0.wireOp",EDGE,"E25.2"),sQuery(id+"F0.wireOp",EDGE,"E25.3"),sQuery(id+"F0.wireOp",EDGE,"E25.4"),sQuery(id+"F0.wireOp",EDGE,"E25.5"),sQuery(id+"F0.wireOp",EDGE,"E25.6"),sQuery(id+"F0.wireOp",EDGE,"E25.7")])],"isStart":false});
            extrude(context, id + "F17", {"entities" : qUnion([Q0, Q1, Q2]), "operationType" : NewBodyOperationType.ADD, "endBound" : BoundingType.UP_TO_SURFACE, "endBoundEntityFace" : qUnion([Q3]), "depth" : 25 * mm});
        }
    });
